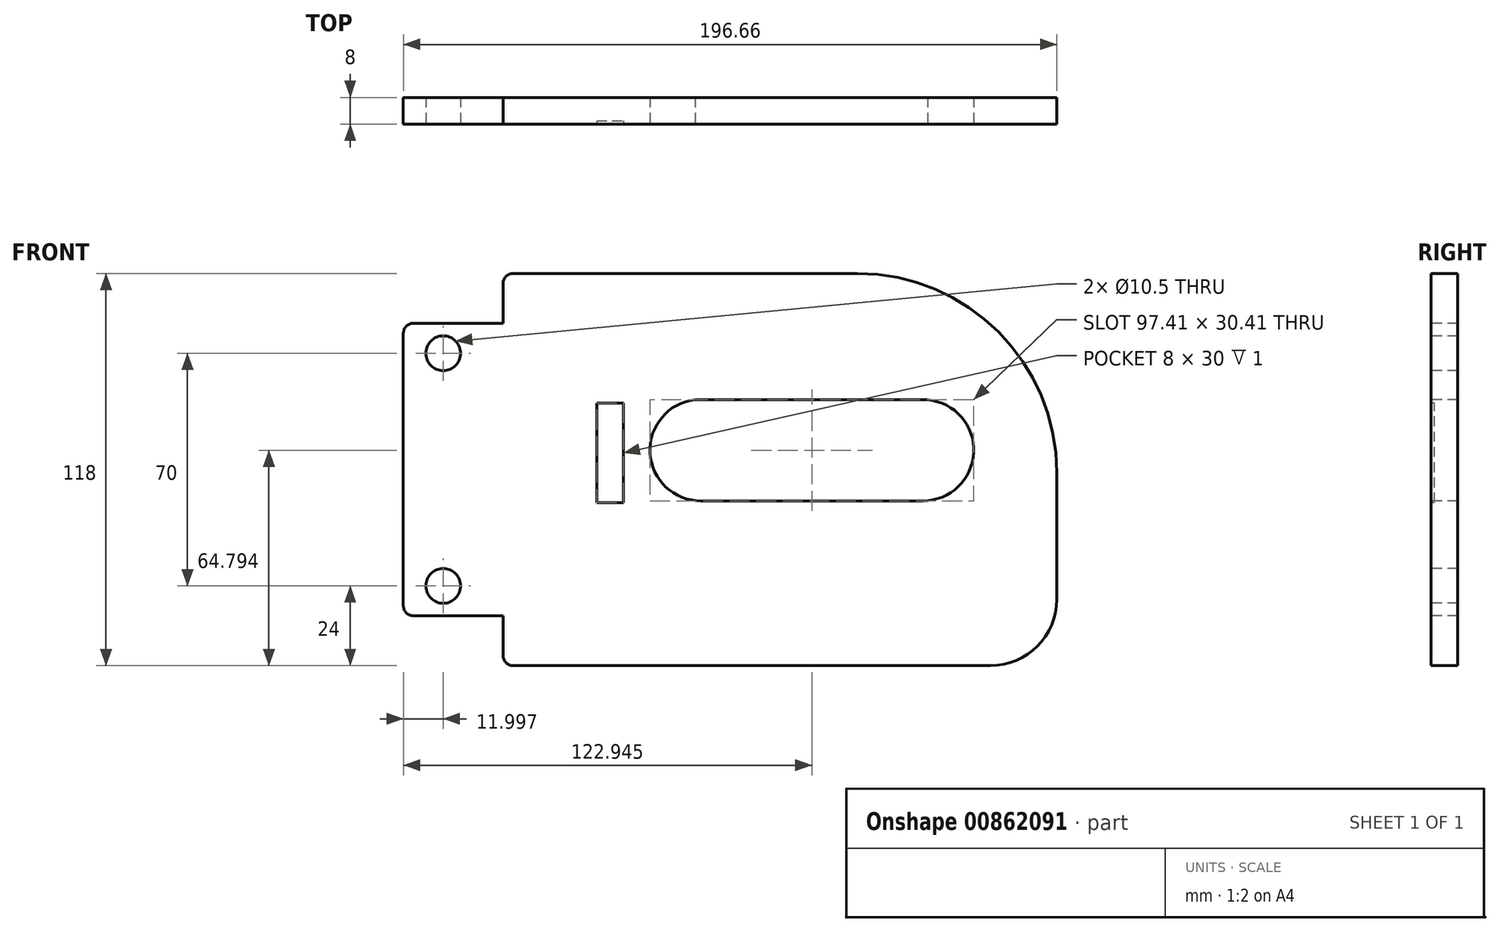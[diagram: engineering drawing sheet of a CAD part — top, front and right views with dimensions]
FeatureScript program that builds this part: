
annotation { "Feature Type Name" : "Feature", "Feature Type Description" : "" }
export const myFeature = defineFeature(function(context is Context, id is Id, definition is map)
    precondition{}
    {
        {
            var Q0;
            Q0=qCreatedBy(makeId("Front.planeOp"),FACE);
            var sketch = newSketch(context, id + "F0", { "sketchPlane" : qUnion([Q0])});
            skLineSegment(sketch, "E0.bottom", {"start": v(78.33, -59) * mm, "end": v(-65.33, -59) * mm});
            skLineSegment(sketch, "E0.top", {"start": v(38.33, 59) * mm, "end": v(-65.33, 59) * mm});
            skLineSegment(sketch, "E0.left", {"start": v(98.33, -39) * mm, "end": v(98.33, -1) * mm});
            skLineSegment(sketch, "E0.right", {"start": v(-98.33, -41) * mm, "end": v(-98.33, 41) * mm});
            skPoint(sketch, "E0.middle", {"position": v(0, 0) * mm});
            skPoint(sketch, "E1.visualSharp", {"position": v(-98.33, -59) * mm});
            skPoint(sketch, "E2.visualSharp", {"position": v(98.33, 59) * mm});
            skPoint(sketch, "E3.visualSharp", {"position": v(98.33, -59) * mm});
            skArc(sketch, "E3.filletArc", {"start": v(78.33, -59) * mm, "mid": v(92.48, -53.14) * mm, "end": v(98.33, -39) * mm});
            skLineSegment(sketch, "E4.bottom", {"start": v(-10.5, 21) * mm, "end": v(59.5, 21) * mm});
            skLineSegment(sketch, "E4.top", {"start": v(-8.86, -9.41) * mm, "end": v(58.1, -9.41) * mm});
            skArc(sketch, "E5", {"start": v(-10.5, 21) * mm, "mid": v(-24.09, 5.02) * mm, "end": v(-8.86, -9.41) * mm});
            skArc(sketch, "E6", {"start": v(58.1, -9.41) * mm, "mid": v(73.32, 5.12) * mm, "end": v(59.5, 21) * mm});
            skArc(sketch, "E7.filletArc", {"start": v(98.33, -1) * mm, "mid": v(80.76, 41.43) * mm, "end": v(38.33, 59) * mm});
            skLineSegment(sketch, "E8", {"start": v(-68.33, 56) * mm, "end": v(-68.33, 44) * mm});
            skLineSegment(sketch, "E9", {"start": v(-68.33, 44) * mm, "end": v(-95.33, 44) * mm});
            skLineSegment(sketch, "E10", {"start": v(-68.33, -56) * mm, "end": v(-68.33, -44) * mm});
            skPoint(sketch, "E11.visualSharp", {"position": v(-68.33, 59) * mm});
            skArc(sketch, "E11.filletArc", {"start": v(-65.33, 59) * mm, "mid": v(-67.45, 58.12) * mm, "end": v(-68.33, 56) * mm});
            skPoint(sketch, "E12.visualSharp", {"position": v(-68.33, -59) * mm});
            skArc(sketch, "E12.filletArc", {"start": v(-68.33, -56) * mm, "mid": v(-67.45, -58.12) * mm, "end": v(-65.33, -59) * mm});
            skPoint(sketch, "E13.visualSharp", {"position": v(-98.33, 44) * mm});
            skArc(sketch, "E13.filletArc", {"start": v(-95.33, 44) * mm, "mid": v(-97.45, 43.12) * mm, "end": v(-98.33, 41) * mm});
            skPoint(sketch, "E14.visualSharp", {"position": v(-98.33, -39) * mm});
            skLineSegment(sketch, "E15", {"start": v(-68.33, -44) * mm, "end": v(-95.33, -44) * mm});
            skArc(sketch, "E16.filletArc", {"start": v(-98.33, -41) * mm, "mid": v(-97.45, -43.12) * mm, "end": v(-95.33, -44) * mm});
            skSolve(sketch);
        }
        {
            var Q0;
            Q0=makeQuery(id+"F0.imprint","IMPRINT",FACE,{"disambiguationData":[TD([[makeQuery(id+"F0.imprint","IMPRINT",EDGE,{"derivedFrom":sQuery(id+"F0.wireOp",EDGE,"E0.bottom")}),-1.0]])]});
            extrude(context, id + "F1", {"entities" : qUnion([Q0]), "oppositeDirection" : true, "depth" : 8 * mm, "offsetDistance" : 25 * mm});
        }
        {
            var Q0;
            Q0=makeQuery(id+"F1.opExtrude","CAP_FACE",FACE,{"disambiguationData":[OSD([sQuery(id+"F0.wireOp",EDGE,"E0.bottom"),sQuery(id+"F0.wireOp",EDGE,"E0.top"),sQuery(id+"F0.wireOp",EDGE,"E0.left"),sQuery(id+"F0.wireOp",EDGE,"E0.right"),sQuery(id+"F0.wireOp",EDGE,"E3.filletArc"),sQuery(id+"F0.wireOp",EDGE,"E4.bottom"),sQuery(id+"F0.wireOp",EDGE,"E4.top"),sQuery(id+"F0.wireOp",EDGE,"E5"),sQuery(id+"F0.wireOp",EDGE,"E6"),sQuery(id+"F0.wireOp",EDGE,"E7.filletArc"),sQuery(id+"F0.wireOp",EDGE,"E8"),sQuery(id+"F0.wireOp",EDGE,"E9"),sQuery(id+"F0.wireOp",EDGE,"E10"),sQuery(id+"F0.wireOp",EDGE,"E11.filletArc"),sQuery(id+"F0.wireOp",EDGE,"E12.filletArc"),sQuery(id+"F0.wireOp",EDGE,"E13.filletArc"),sQuery(id+"F0.wireOp",EDGE,"E15"),sQuery(id+"F0.wireOp",EDGE,"E16.filletArc")])],"isStart":true});
            var sketch = newSketch(context, id + "F2", { "sketchPlane" : qUnion([Q0])});
            skCircle(sketch, "E17", {"center": v(-86.33, 35) * mm, "radius": 5.76 * mm});
            skCircle(sketch, "E18", {"center": v(-86.33, -35) * mm, "radius": 5.46 * mm});
            skSolve(sketch);
        }
        {
            var Q0;
            Q0=sQuery(id+"F2.wireOp",VERTEX,"E17.center");
            var Q1;
            Q1=sQuery(id+"F2.wireOp",VERTEX,"E18.center");
            var Q2;
            Q2=makeQuery(id+"F1.opExtrude","SWEPT_BODY",BODY,{"disambiguationData":[OSD([sQuery(id+"F0.wireOp",EDGE,"E0.bottom"),sQuery(id+"F0.wireOp",EDGE,"E0.top"),sQuery(id+"F0.wireOp",EDGE,"E0.left"),sQuery(id+"F0.wireOp",EDGE,"E0.right"),sQuery(id+"F0.wireOp",EDGE,"E3.filletArc"),sQuery(id+"F0.wireOp",EDGE,"E4.bottom"),sQuery(id+"F0.wireOp",EDGE,"E4.top"),sQuery(id+"F0.wireOp",EDGE,"E5"),sQuery(id+"F0.wireOp",EDGE,"E6"),sQuery(id+"F0.wireOp",EDGE,"E7.filletArc"),sQuery(id+"F0.wireOp",EDGE,"E8"),sQuery(id+"F0.wireOp",EDGE,"E9"),sQuery(id+"F0.wireOp",EDGE,"E10"),sQuery(id+"F0.wireOp",EDGE,"E11.filletArc"),sQuery(id+"F0.wireOp",EDGE,"E12.filletArc"),sQuery(id+"F0.wireOp",EDGE,"E13.filletArc"),sQuery(id+"F0.wireOp",EDGE,"E15"),sQuery(id+"F0.wireOp",EDGE,"E16.filletArc")])]});
            hole(context, id + "F3", {"style" : HoleStyle.SIMPLE, "endStyle" : HoleEndStyle.THROUGH, "standardTappedOrClearance" : lookupTablePath({ "standard" : "ISO", "engagement" : "75%", "pitch" : "1.5 mm", "size" : "M12", "type" : "Tapped" }), "standardBlindInLast" : lookupTablePath({ "standard" : "ISO", "engagement" : "75%", "pitch" : "1.5 mm", "size" : "M12", "type" : "Tapped" }), "holeDiameter" : 10.5 * mm, "majorDiameter" : 12 * mm, "showTappedDepth" : true, "isTappedThrough" : true, "tappedDepth" : 12 * mm, "tapClearance" : 3, "locations" : qUnion([Q0, Q1]), "scope" : qUnion([Q2])});
        }
        {
            var Q0;
            Q0=makeQuery(id+"F1.opExtrude","CAP_FACE",FACE,{"disambiguationData":[OSD([sQuery(id+"F0.wireOp",EDGE,"E0.bottom"),sQuery(id+"F0.wireOp",EDGE,"E0.top"),sQuery(id+"F0.wireOp",EDGE,"E0.left"),sQuery(id+"F0.wireOp",EDGE,"E0.right"),sQuery(id+"F0.wireOp",EDGE,"E3.filletArc"),sQuery(id+"F0.wireOp",EDGE,"E4.bottom"),sQuery(id+"F0.wireOp",EDGE,"E4.top"),sQuery(id+"F0.wireOp",EDGE,"E5"),sQuery(id+"F0.wireOp",EDGE,"E6"),sQuery(id+"F0.wireOp",EDGE,"E7.filletArc"),sQuery(id+"F0.wireOp",EDGE,"E8"),sQuery(id+"F0.wireOp",EDGE,"E9"),sQuery(id+"F0.wireOp",EDGE,"E10"),sQuery(id+"F0.wireOp",EDGE,"E11.filletArc"),sQuery(id+"F0.wireOp",EDGE,"E12.filletArc"),sQuery(id+"F0.wireOp",EDGE,"E13.filletArc"),sQuery(id+"F0.wireOp",EDGE,"E15"),sQuery(id+"F0.wireOp",EDGE,"E16.filletArc")])],"isStart":true});
            var sketch = newSketch(context, id + "F4", { "sketchPlane" : qUnion([Q0])});
            skLineSegment(sketch, "E19.bottom", {"start": v(-40.11, -9.98) * mm, "end": v(-32.11, -9.98) * mm});
            skLineSegment(sketch, "E19.top", {"start": v(-40.11, 20.02) * mm, "end": v(-32.11, 20.02) * mm});
            skLineSegment(sketch, "E19.left", {"start": v(-40.11, -9.98) * mm, "end": v(-40.11, 20.02) * mm});
            skLineSegment(sketch, "E19.right", {"start": v(-32.11, -9.98) * mm, "end": v(-32.11, 20.02) * mm});
            skPoint(sketch, "E19.middle", {"position": v(-36.11, 5.02) * mm});
            skPoint(sketch, "E19.middle.positionSnap0", {"position": v(-24.09, 5.02) * mm});
            skPoint(sketch, "E19.centerSnap0", {"position": v(-24, 5.02) * mm});
            skSolve(sketch);
        }
        {
            var Q0;
            Q0 = qSketchRegion(id + "F4", true);
            extrude(context, id + "F5", {"entities" : qUnion([Q0]), "operationType" : NewBodyOperationType.REMOVE, "oppositeDirection" : true, "depth" : 1 * mm, "offsetDistance" : 25 * mm});
        }
    });
